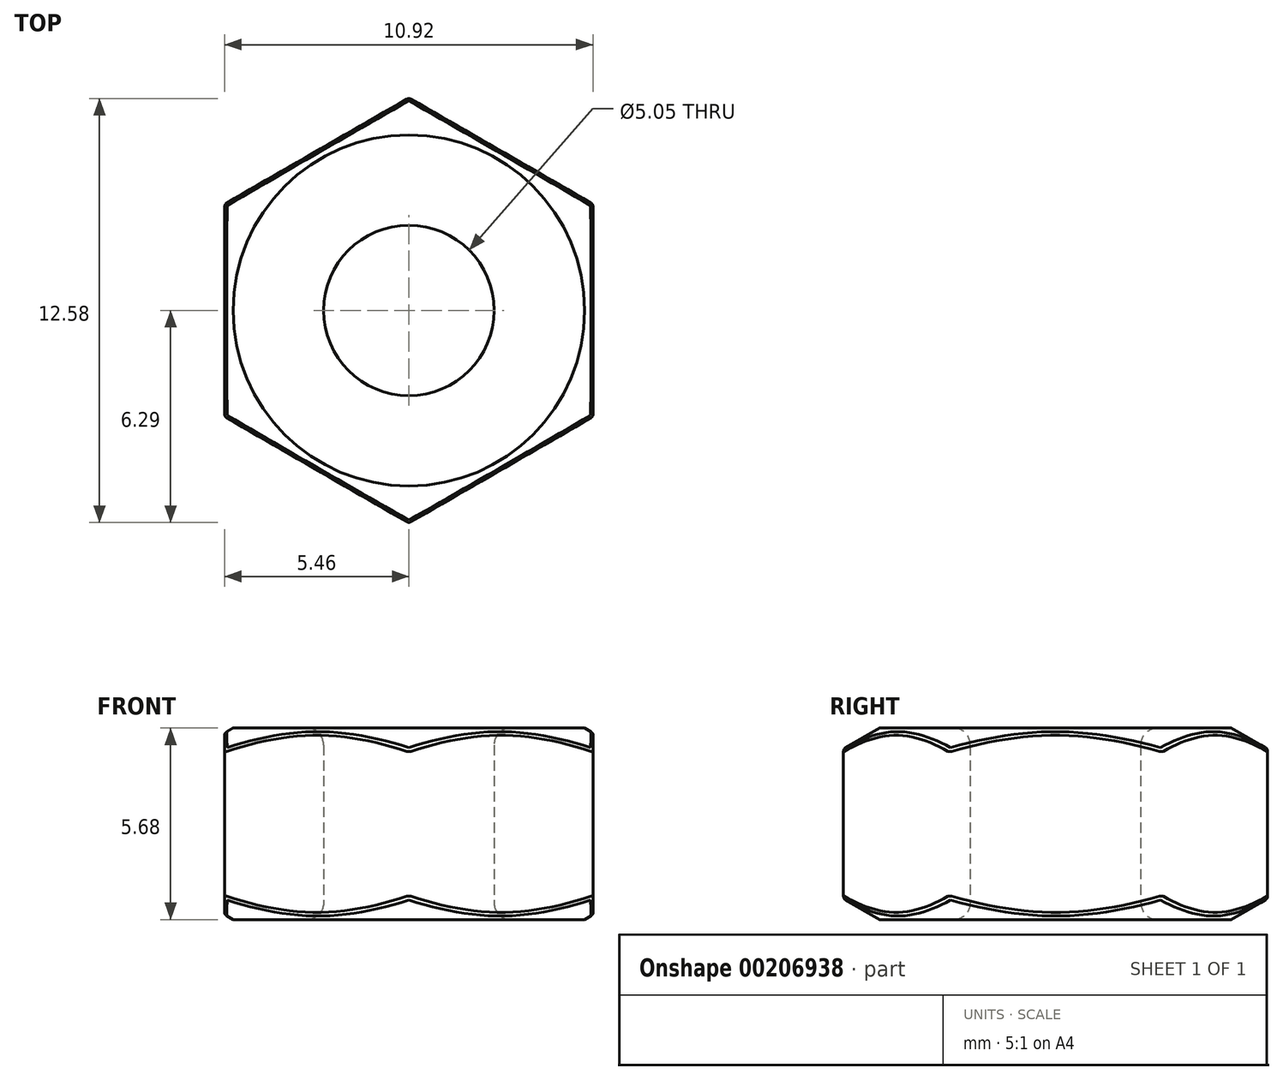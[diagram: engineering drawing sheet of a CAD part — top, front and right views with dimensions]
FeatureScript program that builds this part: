
annotation { "Feature Type Name" : "Feature", "Feature Type Description" : "" }
export const myFeature = defineFeature(function(context is Context, id is Id, definition is map)
    precondition{}
    {
        {
            var Q0;
            Q0=qCreatedBy(makeId("Top.planeOp"),FACE);
            var sketch = newSketch(context, id + "F0", { "sketchPlane" : qUnion([Q0])});
            skCircle(sketch, "E0.cCircle", {"center": v(0, 0) * mm, "radius": 5.46 * mm, "construction": true});
            skLineSegment(sketch, "E0.0", {"start": v(5.46, 3.15) * mm, "end": v(5.46, -3.15) * mm});
            skLineSegment(sketch, "E0.1", {"start": v(5.46, -3.15) * mm, "end": v(0, -6.3) * mm});
            skLineSegment(sketch, "E0.2", {"start": v(0, -6.3) * mm, "end": v(-5.46, -3.15) * mm});
            skLineSegment(sketch, "E0.3", {"start": v(-5.46, -3.15) * mm, "end": v(-5.46, 3.15) * mm});
            skLineSegment(sketch, "E0.4", {"start": v(-5.46, 3.15) * mm, "end": v(0, 6.3) * mm});
            skLineSegment(sketch, "E0.5", {"start": v(0, 6.3) * mm, "end": v(5.46, 3.15) * mm});
            skPoint(sketch, "E0.0.midPoint", {"position": v(5.46, 0) * mm});
            skCircle(sketch, "E1", {"center": v(0, 0) * mm, "radius": 2.53 * mm});
            skSolve(sketch);
        }
        {
            var Q0;
            Q0 = qSketchRegion(id + "F0", true);
            extrude(context, id + "F1", {"entities" : qUnion([Q0]), "endBound" : BoundingType.SYMMETRIC, "depth" : 5.7 * mm});
        }
        {
            var Q0;
            Q0=qCreatedBy(makeId("Front.planeOp"),FACE);
            var sketch = newSketch(context, id + "F2", { "sketchPlane" : qUnion([Q0])});
            skLineSegment(sketch, "E2", {"start": v(5.2, 2.84) * mm, "end": v(7.5, 2.84) * mm});
            skLineSegment(sketch, "E3", {"start": v(7.5, 2.84) * mm, "end": v(7.5, 1.52) * mm});
            skLineSegment(sketch, "E4", {"start": v(7.5, 1.52) * mm, "end": v(5.2, 2.84) * mm});
            skLineSegment(sketch, "E5.MirrorCS", {"start": v(5.2, -2.84) * mm, "end": v(7.5, -2.84) * mm});
            skLineSegment(sketch, "E6.MirrorCS", {"start": v(7.5, -1.52) * mm, "end": v(5.2, -2.84) * mm});
            skLineSegment(sketch, "E7.MirrorCS", {"start": v(7.5, -2.84) * mm, "end": v(7.5, -1.52) * mm});
            skLineSegment(sketch, "E8", {"start": v(0, 4.8) * mm, "end": v(0, -4.77) * mm, "construction": true});
            skSolve(sketch);
        }
        {
            var Q0;
            Q0 = qSketchRegion(id + "F2", true);
            var Q1;
            Q1=sQuery(id+"F2.wireOp",EDGE,"E8");
            revolve(context, id + "F3", {"operationType" : NewBodyOperationType.REMOVE, "entities" : qUnion([Q0]), "axis" : qUnion([Q1]), "revolveType" : RevolveType.FULL, "oppositeDirection" : true});
        }
        {
            var Q0;
            Q0=makeQuery(id+"F1.opExtrude","CAP_EDGE",EDGE,{"disambiguationData":[OSD([sQuery(id+"F0.wireOp",EDGE,"E1")])],"isStart":false});
            var Q1;
            Q1=makeQuery(id+"F1.opExtrude","CAP_EDGE",EDGE,{"disambiguationData":[OSD([sQuery(id+"F0.wireOp",EDGE,"E1")])],"isStart":true});
            fillet(context, id + "F4", {"entities" : qUnion([Q0, Q1]), "radius" : 0.5 * mm, "tangentPropagation" : true, "allowEdgeOverflow" : false});
        }
        {
            var Q0;
            Q0=makeQuery(id+"F3.boolean.opBoolean","COPY",EDGE,{"derivedFrom":makeQuery(id+"F3.opRevolve","SWEPT_EDGE",EDGE,{"disambiguationData":[OSD([sQuery(id+"F2.wireOp",EDGE,"E2"),sQuery(id+"F2.wireOp",EDGE,"E4")])]})});
            var Q1;
            Q1=makeQuery(id+"F1.opExtrude","SWEPT_FACE",FACE,{"disambiguationData":[OSD([sQuery(id+"F0.wireOp",EDGE,"E0.1")])]});
            var Q2;
            Q2=makeQuery(id+"F1.opExtrude","SWEPT_FACE",FACE,{"disambiguationData":[OSD([sQuery(id+"F0.wireOp",EDGE,"E0.2")])]});
            var Q3;
            Q3=makeQuery(id+"F1.opExtrude","SWEPT_FACE",FACE,{"disambiguationData":[OSD([sQuery(id+"F0.wireOp",EDGE,"E0.3")])]});
            var Q4;
            Q4=makeQuery(id+"F1.opExtrude","SWEPT_FACE",FACE,{"disambiguationData":[OSD([sQuery(id+"F0.wireOp",EDGE,"E0.4")])]});
            var Q5;
            Q5=makeQuery(id+"F1.opExtrude","SWEPT_FACE",FACE,{"disambiguationData":[OSD([sQuery(id+"F0.wireOp",EDGE,"E0.5")])]});
            var Q6;
            Q6=makeQuery(id+"F1.opExtrude","SWEPT_FACE",FACE,{"disambiguationData":[OSD([sQuery(id+"F0.wireOp",EDGE,"E0.0")])]});
            fillet(context, id + "F5", {"entities" : qUnion([Q0, Q1, Q2, Q3, Q4, Q5, Q6]), "radius" : 0.13 * mm, "tangentPropagation" : true, "allowEdgeOverflow" : false});
        }
    });
